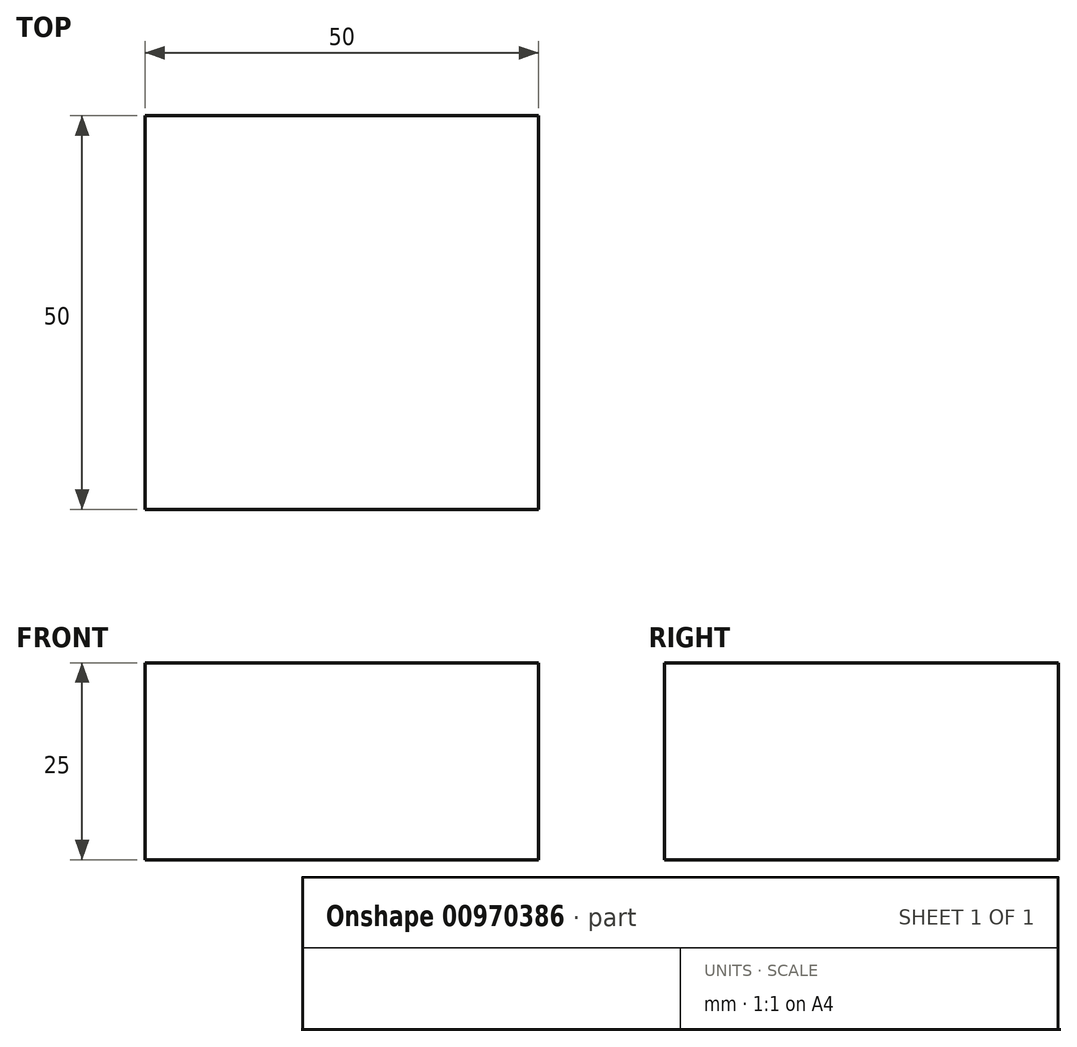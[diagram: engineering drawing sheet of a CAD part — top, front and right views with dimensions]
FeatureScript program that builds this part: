
annotation { "Feature Type Name" : "Feature", "Feature Type Description" : "" }
export const myFeature = defineFeature(function(context is Context, id is Id, definition is map)
    precondition{}
    {
        {
            var Q0;
            Q0=qCreatedBy(makeId("Top.planeOp"),FACE);
            var sketch = newSketch(context, id + "F0", { "sketchPlane" : qUnion([Q0])});
            skLineSegment(sketch, "E0.bottom", {"start": v(-78.44, 76.06) * mm, "end": v(-28.44, 76.06) * mm});
            skLineSegment(sketch, "E0.top", {"start": v(-78.44, 26.06) * mm, "end": v(-28.44, 26.06) * mm});
            skLineSegment(sketch, "E0.left", {"start": v(-78.44, 76.06) * mm, "end": v(-78.44, 26.06) * mm});
            skLineSegment(sketch, "E0.right", {"start": v(-28.44, 76.06) * mm, "end": v(-28.44, 26.06) * mm});
            skSolve(sketch);
        }
        {
            var Q0;
            Q0=makeQuery(id+"F0.imprint","IMPRINT",FACE,{"disambiguationData":[TD([[makeQuery(id+"F0.imprint","IMPRINT",EDGE,{"derivedFrom":sQuery(id+"F0.wireOp",EDGE,"E0.bottom")}),-1.0]])]});
            extrude(context, id + "F1", {"entities" : qUnion([Q0]), "depth" : 25 * mm, "offsetDistance" : 25 * mm});
        }
    });
